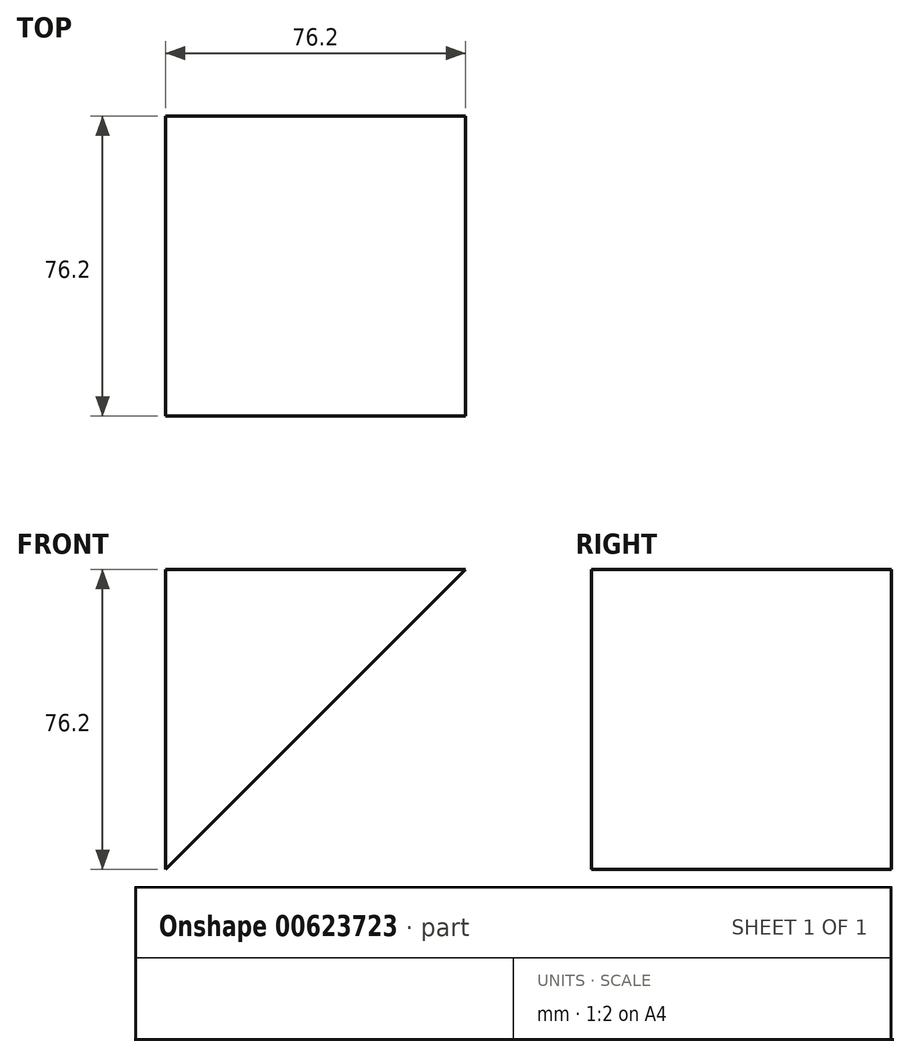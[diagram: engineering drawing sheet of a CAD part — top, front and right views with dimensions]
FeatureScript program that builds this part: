
annotation { "Feature Type Name" : "Feature", "Feature Type Description" : "" }
export const myFeature = defineFeature(function(context is Context, id is Id, definition is map)
    precondition{}
    {
        {
            var Q0;
            Q0=qCreatedBy(makeId("Front.planeOp"),FACE);
            var sketch = newSketch(context, id + "F0", { "sketchPlane" : qUnion([Q0])});
            skLineSegment(sketch, "E0.bottom", {"start": v(38.1, 38.1) * mm, "end": v(-38.1, 38.1) * mm});
            skLineSegment(sketch, "E0.right", {"start": v(-38.1, 38.1) * mm, "end": v(-38.1, -38.1) * mm});
            skPoint(sketch, "E0.middle", {"position": v(0, 0) * mm});
            skLineSegment(sketch, "E1", {"start": v(-38.1, -38.1) * mm, "end": v(38.1, 38.1) * mm});
            skPoint(sketch, "E0.top.start.orphan", {"position": v(38.1, -38.1) * mm});
            skSolve(sketch);
        }
        {
            var Q0;
            Q0 = qSketchRegion(id + "F0", true);
            extrude(context, id + "F1", {"entities" : qUnion([Q0]), "depth" : 76.2 * mm, "offsetDistance" : 25.4 * mm});
        }
    });
